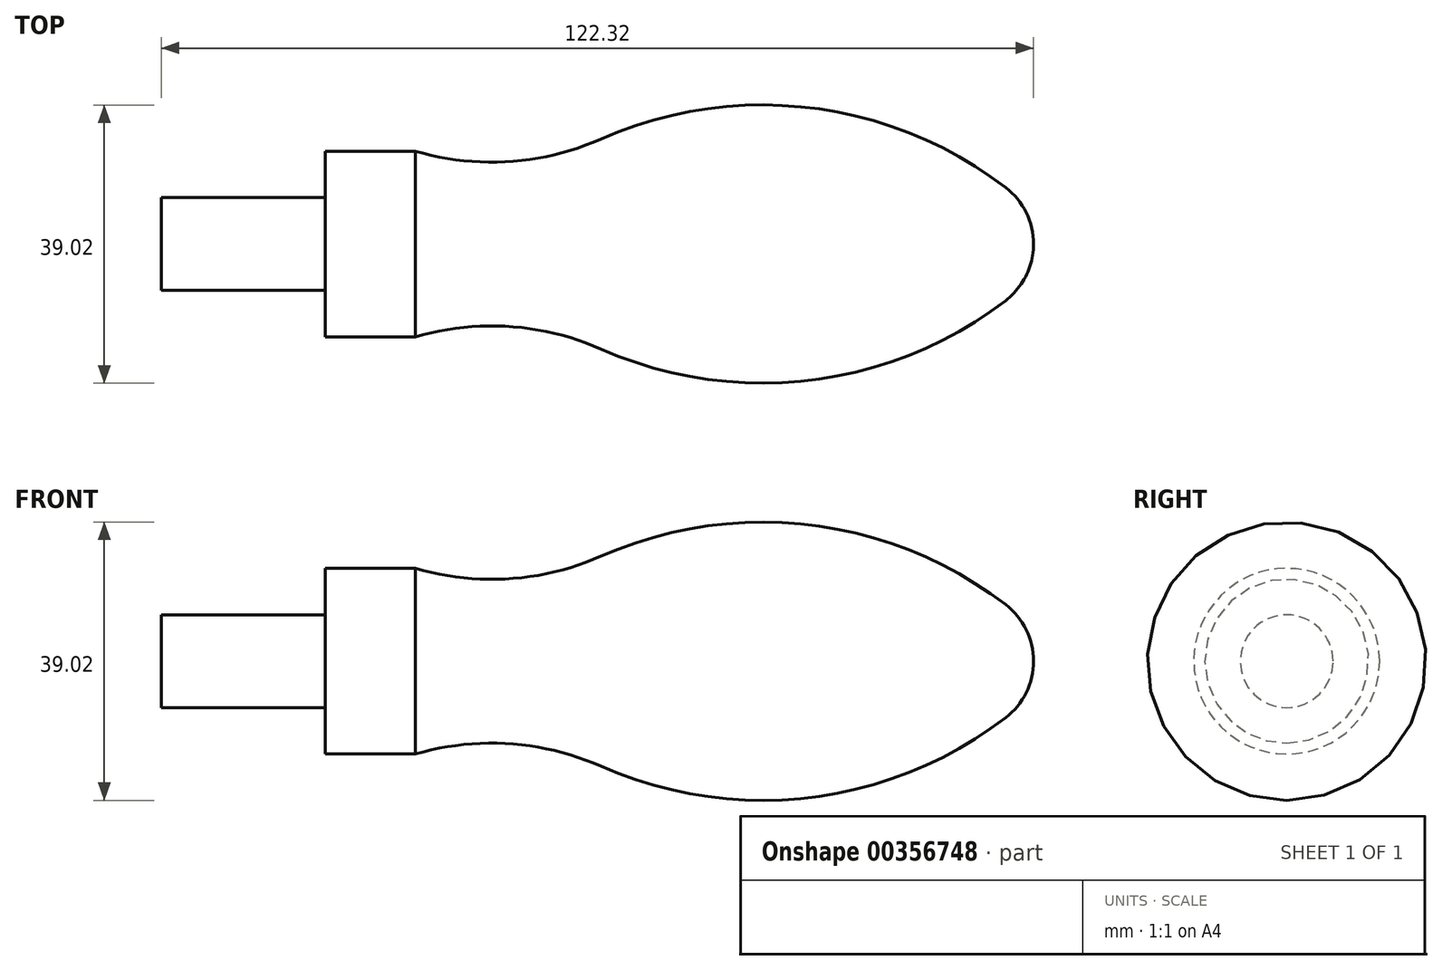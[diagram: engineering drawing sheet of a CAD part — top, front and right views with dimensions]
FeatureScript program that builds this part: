
annotation { "Feature Type Name" : "Feature", "Feature Type Description" : "" }
export const myFeature = defineFeature(function(context is Context, id is Id, definition is map)
    precondition{}
    {
        {
            var Q0;
            Q0=qCreatedBy(makeId("Top.planeOp"),FACE);
            var sketch = newSketch(context, id + "F0", { "sketchPlane" : qUnion([Q0])});
            skArc(sketch, "E0", {"start": v(-22.33, -14.73) * mm, "mid": v(-35.2, -11.57) * mm, "end": v(-48.38, -13.03) * mm});
            skLineSegment(sketch, "E1", {"start": v(67.11, 0) * mm, "end": v(-99.9, 0) * mm});
            skLineSegment(sketch, "E2", {"start": v(-84, 0) * mm, "end": v(-84, -6.5) * mm});
            skLineSegment(sketch, "E3", {"start": v(-84, -6.5) * mm, "end": v(-61, -6.5) * mm});
            skLineSegment(sketch, "E4", {"start": v(-61, 0) * mm, "end": v(-61, -13.03) * mm});
            skLineSegment(sketch, "E5", {"start": v(-61, -13.03) * mm, "end": v(-48, -13.03) * mm});
            skArc(sketch, "E6.trimOffspring", {"start": v(-22.33, -14.73) * mm, "mid": v(6.97, -19.12) * mm, "end": v(34.4, -7.93) * mm});
            skPoint(sketch, "E7.end.orphan", {"position": v(0, 36.13) * mm});
            skArc(sketch, "E8", {"start": v(34.4, -7.93) * mm, "mid": v(37.29, -4.42) * mm, "end": v(38.32, 0) * mm});
            skSolve(sketch);
        }
        {
            var Q0;
            {var subQ7=sQuery(id+"F0.wireOp",EDGE,"E0");Q0=makeQuery(id+"F0.imprint","IMPRINT",FACE,{"disambiguationData":[TD([[makeQuery(id+"F0.imprint","IMPRINT",EDGE,{"derivedFrom":subQ7}),-1.0]])]});}
            var Q1;
            {var subQ0=sQuery(id+"F0.wireOp",EDGE,"E2");Q1=makeQuery(id+"F0.imprint","IMPRINT",FACE,{"disambiguationData":[TD([[makeQuery(id+"F0.imprint","IMPRINT",EDGE,{"derivedFrom":subQ0}),1.0]])]});}
            var Q2;
            Q2=sQuery(id+"F0.wireOp",EDGE,"E1");
            revolve(context, id + "F1", {"entities" : qUnion([Q0, Q1]), "axis" : qUnion([Q2]), "revolveType" : RevolveType.FULL});
        }
    });
